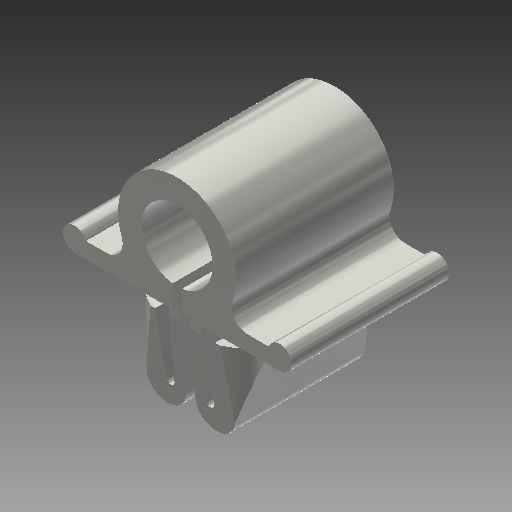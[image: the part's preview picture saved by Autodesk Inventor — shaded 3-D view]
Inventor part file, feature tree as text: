
AUTODESK INVENTOR PART (.ipt)
format: ipt  version: 2019 (Build 230136000, 136)  size: 239,616 bytes
history: native  units: mm
features: extrude x3, sketch x3, projected_geometry x1
ambient origin geometry x8: Origin, YZ Plane, XZ Plane, XY Plane, X Axis, Y Axis, Z Axis, Center Point
bodies: Solid1 (feature_tree)
feature tree (7):
  extrude  "Extrusion1"  Depth=7.5mm
  extrude  "Extrusion2"  Depth=1.0mm
  extrude  "Extrusion3"  Depth=10.0mm
  sketch  "Sketch1"  dims[d0=4.5mm d1=7.5mm]
  sketch  "Sketch2"  dims[d2=3.643mm d3=1.0mm d4=1.0mm]
  sketch  "Sketch3"  dims[d5=1.5mm d6=1.5mm d7=6.5mm d8=6.5mm d9=3.75mm d10=1.0mm d11=0.6mm d12=0.3mm d13=0.5mm d14=2.5mm d15=4.0mm d16=1.0mm d17=2.1mm d18=0.2mm d19=0.7mm d20=5.0mm d21=3.643mm d22=1.0mm d23=1.0mm d24=5.0mm d25=1.0mm d26=10.0mm d27=0.0mm d28=10.0mm d29=5.0mm d30=10.0mm d31=0.0mm d32=1.0mm d33=0.872665mm d34=0.5mm d35=1.0mm d36=8.0mm d37=10.0mm d38=0.0mm]
  projected_geometry  "Projected Loop1"
